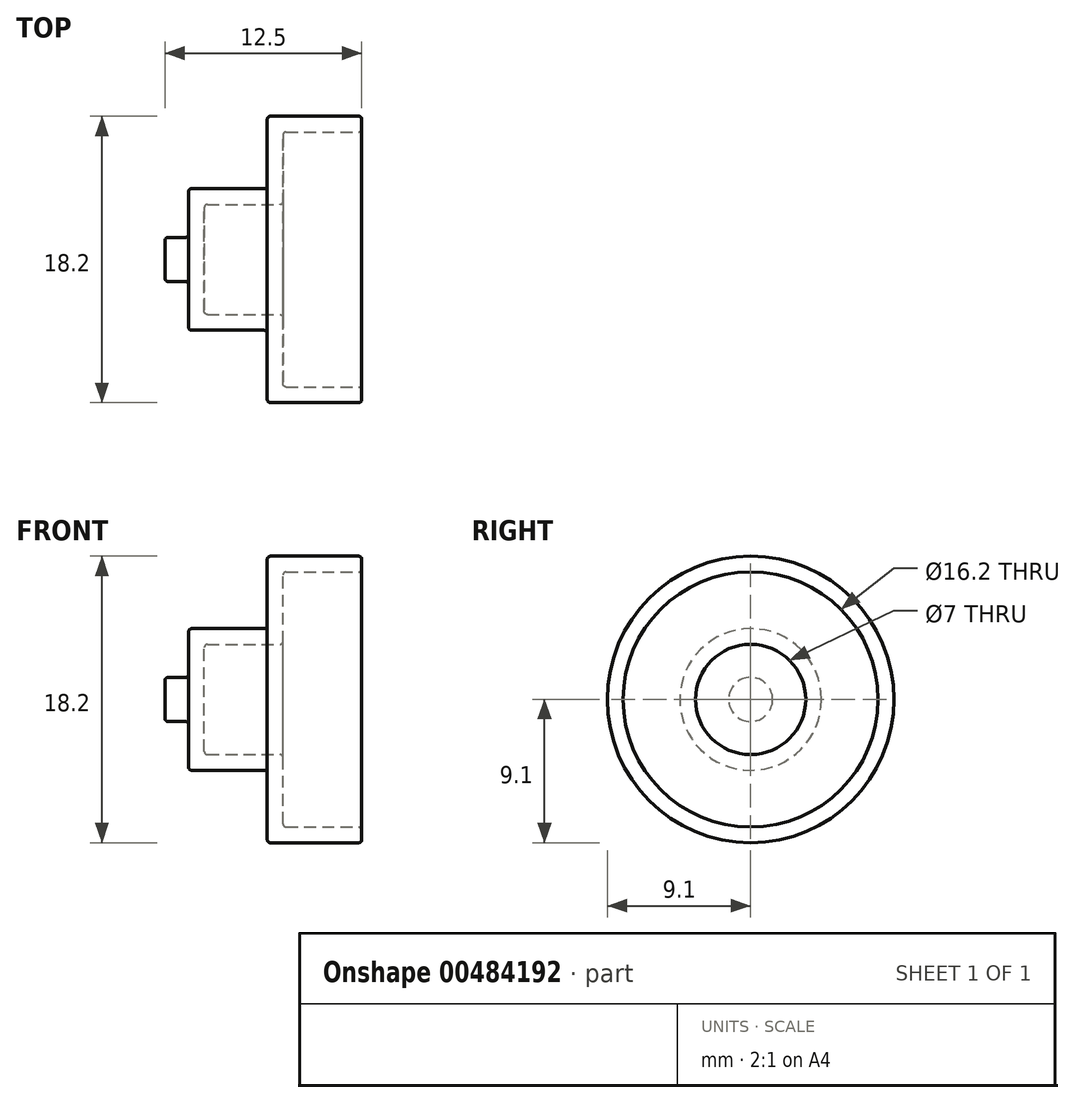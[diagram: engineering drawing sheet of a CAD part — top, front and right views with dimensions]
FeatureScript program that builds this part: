
annotation { "Feature Type Name" : "Feature", "Feature Type Description" : "" }
export const myFeature = defineFeature(function(context is Context, id is Id, definition is map)
    precondition{}
    {
        {
            var Q0;
            Q0=qCreatedBy(makeId("Front.planeOp"),FACE);
            var sketch = newSketch(context, id + "F0", { "sketchPlane" : qUnion([Q0])});
            skLineSegment(sketch, "E0", {"start": v(0, 0) * mm, "end": v(-12.5, 0) * mm});
            skLineSegment(sketch, "E1", {"start": v(-12.5, 0) * mm, "end": v(-12.5, 1.4) * mm});
            skLineSegment(sketch, "E2", {"start": v(-12.5, 1.4) * mm, "end": v(-11, 1.4) * mm});
            skLineSegment(sketch, "E3", {"start": v(-11, 1.4) * mm, "end": v(-11, 4.5) * mm});
            skLineSegment(sketch, "E4", {"start": v(-11, 4.5) * mm, "end": v(-6, 4.5) * mm});
            skLineSegment(sketch, "E5", {"start": v(-6, 4.5) * mm, "end": v(-6, 9.1) * mm});
            skLineSegment(sketch, "E6", {"start": v(-6, 9.1) * mm, "end": v(0, 9.1) * mm});
            skLineSegment(sketch, "E7", {"start": v(0, 9.1) * mm, "end": v(0, 0) * mm});
            skSolve(sketch);
        }
        {
            var Q0;
            Q0=makeQuery(id+"F0.imprint","IMPRINT",FACE,{"disambiguationData":[TD([[makeQuery(id+"F0.imprint","IMPRINT",EDGE,{"derivedFrom":sQuery(id+"F0.wireOp",EDGE,"E0")}),-1.0]])]});
            var Q1;
            Q1=sQuery(id+"F0.wireOp",EDGE,"E0");
            revolve(context, id + "F1", {"surfaceOperationType" : NewSurfaceOperationType.NEW, "entities" : qUnion([Q0]), "axis" : qUnion([Q1]), "revolveType" : RevolveType.FULL});
        }
        {
            var Q0;
            Q0=makeQuery(id+"F1.opRevolve","SWEPT_FACE",FACE,{"disambiguationData":[OSD([sQuery(id+"F0.wireOp",EDGE,"E7")])]});
            shell(context, id + "F2", {"entities" : qUnion([Q0]), "thickness" : 1 * mm});
        }
        {
            var Q0;
            Q0=makeQuery(id+"F2.opShell","OFFSET_FACE",FACE,{"disambiguationData":[OSD([sQuery(id+"F0.wireOp",EDGE,"E1")])]});
            var Q1;
            Q1=makeQuery(id+"F2.opShell","OFFSET_FACE",FACE,{"disambiguationData":[OSD([sQuery(id+"F0.wireOp",EDGE,"E3")])]});
            extrude(context, id + "F3", {"entities" : qUnion([Q0]), "operationType" : NewBodyOperationType.ADD, "endBound" : BoundingType.UP_TO_SURFACE, "depth" : 25 * mm, "endBoundEntityFace" : qUnion([Q1]), "offsetDistance" : 25 * mm});
        }
        {
            var Q0;
            Q0=makeQuery(id+"F1.opRevolve","SWEPT_FACE",FACE,{"disambiguationData":[OSD([sQuery(id+"F0.wireOp",EDGE,"E2")])]});
            var Q1;
            Q1=makeQuery(id+"F1.opRevolve","SWEPT_FACE",FACE,{"disambiguationData":[OSD([sQuery(id+"F0.wireOp",EDGE,"E1")])]});
            var Q2;
            Q2=makeQuery(id+"F1.opRevolve","SWEPT_EDGE",EDGE,{"disambiguationData":[OSD([sQuery(id+"F0.wireOp",EDGE,"E1"),sQuery(id+"F0.wireOp",EDGE,"E2")])]});
            var Q3;
            Q3=makeQuery(id+"F1.opRevolve","SWEPT_FACE",FACE,{"disambiguationData":[OSD([sQuery(id+"F0.wireOp",EDGE,"E5")])]});
            var Q4;
            Q4=makeQuery(id+"F1.opRevolve","SWEPT_FACE",FACE,{"disambiguationData":[OSD([sQuery(id+"F0.wireOp",EDGE,"E4")])]});
            var Q5;
            Q5=makeQuery(id+"F1.opRevolve","SWEPT_FACE",FACE,{"disambiguationData":[OSD([sQuery(id+"F0.wireOp",EDGE,"E3")])]});
            var Q6;
            Q6=makeQuery(id+"F1.opRevolve","SWEPT_EDGE",EDGE,{"disambiguationData":[OSD([sQuery(id+"F0.wireOp",EDGE,"E6"),sQuery(id+"F0.wireOp",EDGE,"E7")])]});
            var Q7;
            Q7=makeQuery(id+"F1.opRevolve","SWEPT_EDGE",EDGE,{"disambiguationData":[OSD([sQuery(id+"F0.wireOp",EDGE,"E5"),sQuery(id+"F0.wireOp",EDGE,"E6")])]});
            var Q8;
            Q8=makeQuery(id+"F1.opRevolve","SWEPT_EDGE",EDGE,{"disambiguationData":[OSD([sQuery(id+"F0.wireOp",EDGE,"E3"),sQuery(id+"F0.wireOp",EDGE,"E4")])]});
            var Q9;
            Q9=makeQuery(id+"F1.opRevolve","SWEPT_EDGE",EDGE,{"disambiguationData":[OSD([sQuery(id+"F0.wireOp",EDGE,"E4"),sQuery(id+"F0.wireOp",EDGE,"E5")])]});
            var Q10;
            Q10=makeQuery(id+"F1.opRevolve","SWEPT_FACE",FACE,{"disambiguationData":[OSD([sQuery(id+"F0.wireOp",EDGE,"E6")])]});
            var Q11;
            Q11=makeQuery(id+"F1.opRevolve","SWEPT_FACE",FACE,{"disambiguationData":[OSD([sQuery(id+"F0.wireOp",EDGE,"E7")])]});
            var Q12;
            Q12=makeQuery(id+"F1.opRevolve","SWEPT_EDGE",EDGE,{"disambiguationData":[OSD([sQuery(id+"F0.wireOp",EDGE,"E2"),sQuery(id+"F0.wireOp",EDGE,"E3")])]});
            var Q13;
            Q13=makeQuery(id+"F2.opShell","OFFSET_EDGE",EDGE,{"disambiguationData":[OSD([sQuery(id+"F0.wireOp",EDGE,"E3"),sQuery(id+"F0.wireOp",EDGE,"E4")])]});
            var Q14;
            Q14=makeQuery(id+"F2.opShell","OFFSET_FACE",FACE,{"disambiguationData":[OSD([sQuery(id+"F0.wireOp",EDGE,"E3")])]});
            var Q15;
            Q15=makeQuery(id+"F2.opShell","OFFSET_EDGE",EDGE,{"disambiguationData":[OSD([sQuery(id+"F0.wireOp",EDGE,"E4"),sQuery(id+"F0.wireOp",EDGE,"E5")])]});
            var Q16;
            Q16=makeQuery(id+"F2.opShell","OFFSET_FACE",FACE,{"disambiguationData":[OSD([sQuery(id+"F0.wireOp",EDGE,"E4")])]});
            var Q17;
            Q17=makeQuery(id+"F2.opShell","OFFSET_EDGE",EDGE,{"disambiguationData":[OSD([sQuery(id+"F0.wireOp",EDGE,"E5"),sQuery(id+"F0.wireOp",EDGE,"E6")])]});
            var Q18;
            Q18=makeQuery(id+"F2.opShell","OFFSET_FACE",FACE,{"disambiguationData":[OSD([sQuery(id+"F0.wireOp",EDGE,"E5")])]});
            var Q19;
            Q19=makeQuery(id+"F2.opShell","OFFSET_EDGE",EDGE,{"disambiguationData":[OSD([sQuery(id+"F0.wireOp",EDGE,"E6"),sQuery(id+"F0.wireOp",EDGE,"E7")])]});
            var Q20;
            Q20=makeQuery(id+"F2.opShell","OFFSET_FACE",FACE,{"disambiguationData":[OSD([sQuery(id+"F0.wireOp",EDGE,"E6")])]});
            fillet(context, id + "F4", {"entities" : qUnion([Q0, Q1, Q2, Q3, Q4, Q5, Q6, Q7, Q8, Q9, Q10, Q11, Q12, Q13, Q14, Q15, Q16, Q17, Q18, Q19, Q20]), "radius" : 0.2 * mm, "tangentPropagation" : true, "allowEdgeOverflow" : false});
        }
    });
